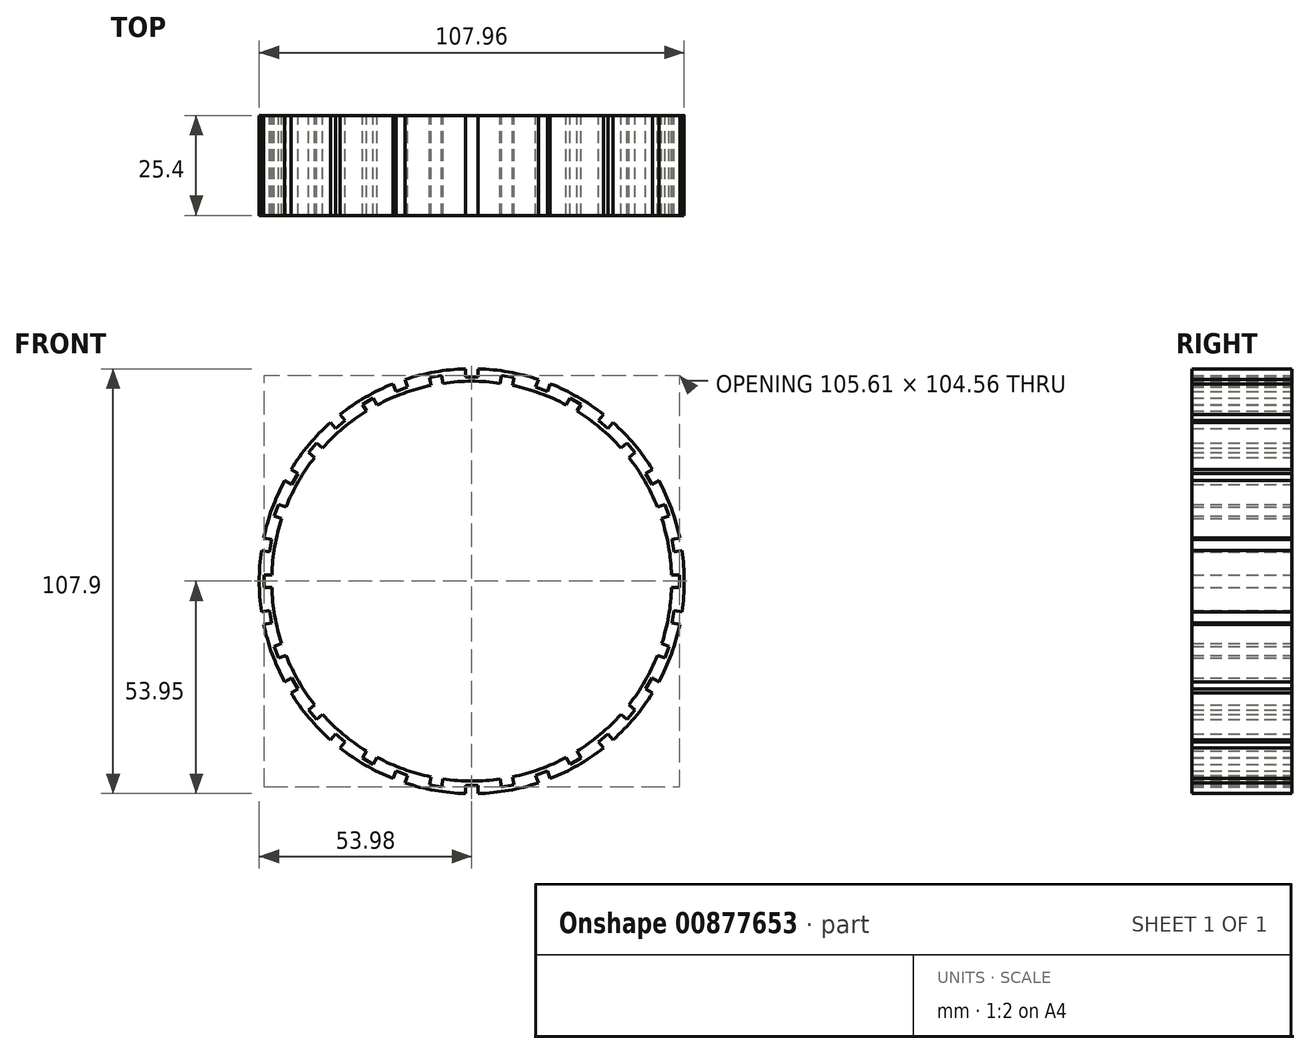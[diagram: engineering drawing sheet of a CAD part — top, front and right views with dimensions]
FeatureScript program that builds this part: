
annotation { "Feature Type Name" : "Feature", "Feature Type Description" : "" }
export const myFeature = defineFeature(function(context is Context, id is Id, definition is map)
    precondition{}
    {
        {
            var Q0;
            Q0=qCreatedBy(makeId("Front.planeOp"),FACE);
            var sketch = newSketch(context, id + "F0", { "sketchPlane" : qUnion([Q0])});
            skArc(sketch, "E0", {"start": v(-1.59, 53.95) * mm, "mid": v(-9.37, 53.15) * mm, "end": v(-16.96, 51.24) * mm});
            skArc(sketch, "E1", {"start": v(-50.78, -1.59) * mm, "mid": v(-50.03, -8.82) * mm, "end": v(-48.26, -15.87) * mm});
            skLineSegment(sketch, "E2", {"start": v(-1.59, 53.95) * mm, "end": v(-1.59, 51.92) * mm});
            skLineSegment(sketch, "E3", {"start": v(-1.59, 51.92) * mm, "end": v(1.59, 51.92) * mm});
            skLineSegment(sketch, "E4", {"start": v(1.59, 51.92) * mm, "end": v(1.59, 53.95) * mm});
            skLineSegment(sketch, "E5.1.0", {"start": v(-19.25, 48.25) * mm, "end": v(-16.27, 49.33) * mm});
            skLineSegment(sketch, "E5.1.1", {"start": v(-16.27, 49.33) * mm, "end": v(-16.96, 51.24) * mm});
            skLineSegment(sketch, "E5.1.2", {"start": v(-19.94, 50.16) * mm, "end": v(-19.25, 48.25) * mm});
            skLineSegment(sketch, "E5.2.0", {"start": v(-34.59, 38.75) * mm, "end": v(-32.16, 40.8) * mm});
            skLineSegment(sketch, "E5.2.1", {"start": v(-32.16, 40.8) * mm, "end": v(-33.46, 42.35) * mm});
            skLineSegment(sketch, "E5.2.2", {"start": v(-35.9, 40.3) * mm, "end": v(-34.59, 38.75) * mm});
            skLineSegment(sketch, "E5.3.0", {"start": v(-45.76, 24.59) * mm, "end": v(-44.17, 27.33) * mm});
            skLineSegment(sketch, "E5.3.1", {"start": v(-44.17, 27.33) * mm, "end": v(-45.93, 28.35) * mm});
            skLineSegment(sketch, "E5.3.2", {"start": v(-47.52, 25.6) * mm, "end": v(-45.76, 24.59) * mm});
            skLineSegment(sketch, "E5.4.0", {"start": v(-51.4, 7.45) * mm, "end": v(-50.86, 10.58) * mm});
            skLineSegment(sketch, "E5.4.1", {"start": v(-50.86, 10.58) * mm, "end": v(-52.86, 10.93) * mm});
            skLineSegment(sketch, "E5.4.2", {"start": v(-53.4, 7.8) * mm, "end": v(-51.4, 7.45) * mm});
            skLineSegment(sketch, "E5.5.0", {"start": v(-50.86, -10.58) * mm, "end": v(-51.4, -7.45) * mm});
            skLineSegment(sketch, "E5.5.1", {"start": v(-51.4, -7.45) * mm, "end": v(-53.4, -7.8) * mm});
            skLineSegment(sketch, "E5.5.2", {"start": v(-52.86, -10.93) * mm, "end": v(-50.86, -10.58) * mm});
            skLineSegment(sketch, "E5.6.0", {"start": v(-44.17, -27.33) * mm, "end": v(-45.76, -24.59) * mm});
            skLineSegment(sketch, "E5.6.1", {"start": v(-45.76, -24.59) * mm, "end": v(-47.52, -25.6) * mm});
            skLineSegment(sketch, "E5.6.2", {"start": v(-45.93, -28.35) * mm, "end": v(-44.17, -27.33) * mm});
            skLineSegment(sketch, "E5.7.0", {"start": v(-32.16, -40.8) * mm, "end": v(-34.59, -38.75) * mm});
            skLineSegment(sketch, "E5.7.1", {"start": v(-34.59, -38.75) * mm, "end": v(-35.9, -40.3) * mm});
            skLineSegment(sketch, "E5.7.2", {"start": v(-33.46, -42.35) * mm, "end": v(-32.16, -40.8) * mm});
            skLineSegment(sketch, "E5.8.0", {"start": v(-16.27, -49.33) * mm, "end": v(-19.25, -48.25) * mm});
            skLineSegment(sketch, "E5.8.1", {"start": v(-19.25, -48.25) * mm, "end": v(-19.94, -50.16) * mm});
            skLineSegment(sketch, "E5.8.2", {"start": v(-16.96, -51.24) * mm, "end": v(-16.27, -49.33) * mm});
            skLineSegment(sketch, "E5.9.0", {"start": v(1.59, -51.92) * mm, "end": v(-1.59, -51.92) * mm});
            skLineSegment(sketch, "E5.9.1", {"start": v(-1.59, -51.92) * mm, "end": v(-1.59, -53.95) * mm});
            skLineSegment(sketch, "E5.9.2", {"start": v(1.59, -53.95) * mm, "end": v(1.59, -51.92) * mm});
            skLineSegment(sketch, "E5.10.0", {"start": v(19.25, -48.25) * mm, "end": v(16.27, -49.33) * mm});
            skLineSegment(sketch, "E5.10.1", {"start": v(16.27, -49.33) * mm, "end": v(16.96, -51.24) * mm});
            skLineSegment(sketch, "E5.10.2", {"start": v(19.94, -50.16) * mm, "end": v(19.25, -48.25) * mm});
            skLineSegment(sketch, "E5.11.0", {"start": v(34.59, -38.75) * mm, "end": v(32.16, -40.8) * mm});
            skLineSegment(sketch, "E5.11.1", {"start": v(32.16, -40.8) * mm, "end": v(33.46, -42.35) * mm});
            skLineSegment(sketch, "E5.11.2", {"start": v(35.9, -40.3) * mm, "end": v(34.59, -38.75) * mm});
            skLineSegment(sketch, "E5.12.0", {"start": v(45.76, -24.59) * mm, "end": v(44.17, -27.33) * mm});
            skLineSegment(sketch, "E5.12.1", {"start": v(44.17, -27.33) * mm, "end": v(45.93, -28.35) * mm});
            skLineSegment(sketch, "E5.12.2", {"start": v(47.52, -25.6) * mm, "end": v(45.76, -24.59) * mm});
            skLineSegment(sketch, "E5.13.0", {"start": v(51.4, -7.45) * mm, "end": v(50.86, -10.58) * mm});
            skLineSegment(sketch, "E5.13.1", {"start": v(50.86, -10.58) * mm, "end": v(52.86, -10.93) * mm});
            skLineSegment(sketch, "E5.13.2", {"start": v(53.4, -7.8) * mm, "end": v(51.4, -7.45) * mm});
            skLineSegment(sketch, "E5.14.0", {"start": v(50.86, 10.58) * mm, "end": v(51.4, 7.45) * mm});
            skLineSegment(sketch, "E5.14.1", {"start": v(51.4, 7.45) * mm, "end": v(53.4, 7.8) * mm});
            skLineSegment(sketch, "E5.14.2", {"start": v(52.86, 10.93) * mm, "end": v(50.86, 10.58) * mm});
            skLineSegment(sketch, "E5.15.0", {"start": v(44.17, 27.33) * mm, "end": v(45.76, 24.59) * mm});
            skLineSegment(sketch, "E5.15.1", {"start": v(45.76, 24.59) * mm, "end": v(47.52, 25.6) * mm});
            skLineSegment(sketch, "E5.15.2", {"start": v(45.93, 28.35) * mm, "end": v(44.17, 27.33) * mm});
            skLineSegment(sketch, "E5.16.0", {"start": v(32.16, 40.8) * mm, "end": v(34.59, 38.75) * mm});
            skLineSegment(sketch, "E5.16.1", {"start": v(34.59, 38.75) * mm, "end": v(35.9, 40.3) * mm});
            skLineSegment(sketch, "E5.16.2", {"start": v(33.46, 42.35) * mm, "end": v(32.16, 40.8) * mm});
            skLineSegment(sketch, "E5.17.0", {"start": v(16.27, 49.33) * mm, "end": v(19.25, 48.25) * mm});
            skLineSegment(sketch, "E5.17.1", {"start": v(19.25, 48.25) * mm, "end": v(19.94, 50.16) * mm});
            skLineSegment(sketch, "E5.17.2", {"start": v(16.96, 51.24) * mm, "end": v(16.27, 49.33) * mm});
            skArc(sketch, "E6.trimOffspring", {"start": v(16.96, 51.24) * mm, "mid": v(9.37, 53.15) * mm, "end": v(1.59, 53.95) * mm});
            skArc(sketch, "E7.trimOffspring", {"start": v(33.46, 42.35) * mm, "mid": v(26.99, 46.74) * mm, "end": v(19.94, 50.16) * mm});
            skArc(sketch, "E8.trimOffspring", {"start": v(45.93, 28.35) * mm, "mid": v(41.35, 34.7) * mm, "end": v(35.9, 40.3) * mm});
            skArc(sketch, "E9.trimOffspring", {"start": v(52.86, 10.93) * mm, "mid": v(50.72, 18.46) * mm, "end": v(47.52, 25.6) * mm});
            skArc(sketch, "E10.trimOffspring", {"start": v(53.4, -7.8) * mm, "mid": v(53.97, 0) * mm, "end": v(53.4, 7.8) * mm});
            skArc(sketch, "E11.trimOffspring", {"start": v(47.52, -25.6) * mm, "mid": v(50.72, -18.46) * mm, "end": v(52.86, -10.93) * mm});
            skArc(sketch, "E12.trimOffspring", {"start": v(35.9, -40.3) * mm, "mid": v(41.35, -34.7) * mm, "end": v(45.93, -28.35) * mm});
            skArc(sketch, "E13.trimOffspring", {"start": v(19.94, -50.16) * mm, "mid": v(26.99, -46.74) * mm, "end": v(33.46, -42.35) * mm});
            skArc(sketch, "E14.trimOffspring", {"start": v(1.59, -53.95) * mm, "mid": v(9.37, -53.15) * mm, "end": v(16.96, -51.24) * mm});
            skArc(sketch, "E15.trimOffspring", {"start": v(-16.96, -51.24) * mm, "mid": v(-9.37, -53.15) * mm, "end": v(-1.59, -53.95) * mm});
            skArc(sketch, "E16.trimOffspring", {"start": v(-33.46, -42.35) * mm, "mid": v(-26.99, -46.74) * mm, "end": v(-19.94, -50.16) * mm});
            skArc(sketch, "E17.trimOffspring", {"start": v(-45.93, -28.35) * mm, "mid": v(-41.35, -34.7) * mm, "end": v(-35.9, -40.3) * mm});
            skArc(sketch, "E18.trimOffspring", {"start": v(-52.86, -10.93) * mm, "mid": v(-50.72, -18.46) * mm, "end": v(-47.52, -25.6) * mm});
            skArc(sketch, "E19.trimOffspring", {"start": v(-53.4, 7.8) * mm, "mid": v(-53.97, 0) * mm, "end": v(-53.4, -7.8) * mm});
            skArc(sketch, "E20.trimOffspring", {"start": v(-47.52, 25.6) * mm, "mid": v(-50.72, 18.46) * mm, "end": v(-52.86, 10.93) * mm});
            skArc(sketch, "E21.trimOffspring", {"start": v(-35.9, 40.3) * mm, "mid": v(-41.35, 34.7) * mm, "end": v(-45.93, 28.35) * mm});
            skArc(sketch, "E22.trimOffspring", {"start": v(-19.94, 50.16) * mm, "mid": v(-26.99, 46.74) * mm, "end": v(-33.46, 42.35) * mm});
            skLineSegment(sketch, "E23", {"start": v(-50.78, 1.59) * mm, "end": v(-52.8, 1.59) * mm});
            skLineSegment(sketch, "E24", {"start": v(-52.8, 1.59) * mm, "end": v(-52.8, -1.59) * mm});
            skLineSegment(sketch, "E25", {"start": v(-52.8, -1.59) * mm, "end": v(-50.78, -1.59) * mm});
            skLineSegment(sketch, "E26.1.0", {"start": v(-49.08, -19.55) * mm, "end": v(-47.17, -18.86) * mm});
            skLineSegment(sketch, "E26.1.1", {"start": v(-50.17, -16.57) * mm, "end": v(-49.08, -19.55) * mm});
            skLineSegment(sketch, "E26.1.2", {"start": v(-48.26, -15.87) * mm, "end": v(-50.17, -16.57) * mm});
            skLineSegment(sketch, "E26.2.0", {"start": v(-39.43, -35.16) * mm, "end": v(-37.88, -33.85) * mm});
            skLineSegment(sketch, "E26.2.1", {"start": v(-41.47, -32.73) * mm, "end": v(-39.43, -35.16) * mm});
            skLineSegment(sketch, "E26.2.2", {"start": v(-39.92, -31.42) * mm, "end": v(-41.47, -32.73) * mm});
            skLineSegment(sketch, "E26.3.0", {"start": v(-25.03, -46.53) * mm, "end": v(-24.01, -44.77) * mm});
            skLineSegment(sketch, "E26.3.1", {"start": v(-27.78, -44.94) * mm, "end": v(-25.03, -46.53) * mm});
            skLineSegment(sketch, "E26.3.2", {"start": v(-26.76, -43.18) * mm, "end": v(-27.78, -44.94) * mm});
            skLineSegment(sketch, "E26.4.0", {"start": v(-7.6, -52.28) * mm, "end": v(-7.25, -50.28) * mm});
            skLineSegment(sketch, "E26.4.1", {"start": v(-10.73, -51.73) * mm, "end": v(-7.6, -52.28) * mm});
            skLineSegment(sketch, "E26.4.2", {"start": v(-10.38, -49.73) * mm, "end": v(-10.73, -51.73) * mm});
            skLineSegment(sketch, "E26.5.0", {"start": v(10.73, -51.73) * mm, "end": v(10.38, -49.73) * mm});
            skLineSegment(sketch, "E26.5.1", {"start": v(7.6, -52.28) * mm, "end": v(10.73, -51.73) * mm});
            skLineSegment(sketch, "E26.5.2", {"start": v(7.25, -50.28) * mm, "end": v(7.6, -52.28) * mm});
            skLineSegment(sketch, "E26.6.0", {"start": v(27.78, -44.94) * mm, "end": v(26.76, -43.18) * mm});
            skLineSegment(sketch, "E26.6.1", {"start": v(25.03, -46.53) * mm, "end": v(27.78, -44.94) * mm});
            skLineSegment(sketch, "E26.6.2", {"start": v(24.01, -44.77) * mm, "end": v(25.03, -46.53) * mm});
            skLineSegment(sketch, "E26.7.0", {"start": v(41.47, -32.73) * mm, "end": v(39.92, -31.42) * mm});
            skLineSegment(sketch, "E26.7.1", {"start": v(39.43, -35.16) * mm, "end": v(41.47, -32.73) * mm});
            skLineSegment(sketch, "E26.7.2", {"start": v(37.88, -33.85) * mm, "end": v(39.43, -35.16) * mm});
            skLineSegment(sketch, "E26.8.0", {"start": v(50.17, -16.57) * mm, "end": v(48.26, -15.87) * mm});
            skLineSegment(sketch, "E26.8.1", {"start": v(49.08, -19.55) * mm, "end": v(50.17, -16.57) * mm});
            skLineSegment(sketch, "E26.8.2", {"start": v(47.17, -18.86) * mm, "end": v(49.08, -19.55) * mm});
            skLineSegment(sketch, "E26.9.0", {"start": v(52.8, 1.59) * mm, "end": v(50.78, 1.59) * mm});
            skLineSegment(sketch, "E26.9.1", {"start": v(52.8, -1.59) * mm, "end": v(52.8, 1.59) * mm});
            skLineSegment(sketch, "E26.9.2", {"start": v(50.78, -1.59) * mm, "end": v(52.8, -1.59) * mm});
            skLineSegment(sketch, "E26.10.0", {"start": v(49.08, 19.55) * mm, "end": v(47.17, 18.86) * mm});
            skLineSegment(sketch, "E26.10.1", {"start": v(50.17, 16.57) * mm, "end": v(49.08, 19.55) * mm});
            skLineSegment(sketch, "E26.10.2", {"start": v(48.26, 15.87) * mm, "end": v(50.17, 16.57) * mm});
            skLineSegment(sketch, "E26.11.0", {"start": v(39.43, 35.16) * mm, "end": v(37.88, 33.85) * mm});
            skLineSegment(sketch, "E26.11.1", {"start": v(41.47, 32.73) * mm, "end": v(39.43, 35.16) * mm});
            skLineSegment(sketch, "E26.11.2", {"start": v(39.92, 31.42) * mm, "end": v(41.47, 32.73) * mm});
            skLineSegment(sketch, "E26.12.0", {"start": v(25.03, 46.53) * mm, "end": v(24.01, 44.77) * mm});
            skLineSegment(sketch, "E26.12.1", {"start": v(27.78, 44.94) * mm, "end": v(25.03, 46.53) * mm});
            skLineSegment(sketch, "E26.12.2", {"start": v(26.76, 43.18) * mm, "end": v(27.78, 44.94) * mm});
            skLineSegment(sketch, "E26.13.0", {"start": v(7.6, 52.28) * mm, "end": v(7.25, 50.28) * mm});
            skLineSegment(sketch, "E26.13.1", {"start": v(10.73, 51.73) * mm, "end": v(7.6, 52.28) * mm});
            skLineSegment(sketch, "E26.13.2", {"start": v(10.38, 49.73) * mm, "end": v(10.73, 51.73) * mm});
            skLineSegment(sketch, "E26.14.0", {"start": v(-10.73, 51.73) * mm, "end": v(-10.38, 49.73) * mm});
            skLineSegment(sketch, "E26.14.1", {"start": v(-7.6, 52.28) * mm, "end": v(-10.73, 51.73) * mm});
            skLineSegment(sketch, "E26.14.2", {"start": v(-7.25, 50.28) * mm, "end": v(-7.6, 52.28) * mm});
            skLineSegment(sketch, "E26.15.0", {"start": v(-27.78, 44.94) * mm, "end": v(-26.76, 43.18) * mm});
            skLineSegment(sketch, "E26.15.1", {"start": v(-25.03, 46.53) * mm, "end": v(-27.78, 44.94) * mm});
            skLineSegment(sketch, "E26.15.2", {"start": v(-24.01, 44.77) * mm, "end": v(-25.03, 46.53) * mm});
            skLineSegment(sketch, "E26.16.0", {"start": v(-41.47, 32.73) * mm, "end": v(-39.92, 31.42) * mm});
            skLineSegment(sketch, "E26.16.1", {"start": v(-39.43, 35.16) * mm, "end": v(-41.47, 32.73) * mm});
            skLineSegment(sketch, "E26.16.2", {"start": v(-37.88, 33.85) * mm, "end": v(-39.43, 35.16) * mm});
            skLineSegment(sketch, "E26.17.0", {"start": v(-50.17, 16.57) * mm, "end": v(-48.26, 15.87) * mm});
            skLineSegment(sketch, "E26.17.1", {"start": v(-49.08, 19.55) * mm, "end": v(-50.17, 16.57) * mm});
            skLineSegment(sketch, "E26.17.2", {"start": v(-47.17, 18.86) * mm, "end": v(-49.08, 19.55) * mm});
            skArc(sketch, "E27.trimOffspring", {"start": v(-48.26, 15.87) * mm, "mid": v(-50.03, 8.82) * mm, "end": v(-50.78, 1.59) * mm});
            skArc(sketch, "E28.trimOffspring", {"start": v(-39.92, 31.42) * mm, "mid": v(-44, 25.4) * mm, "end": v(-47.17, 18.86) * mm});
            skArc(sketch, "E29.trimOffspring", {"start": v(-26.76, 43.18) * mm, "mid": v(-32.65, 38.92) * mm, "end": v(-37.88, 33.85) * mm});
            skArc(sketch, "E30.trimOffspring", {"start": v(-10.38, 49.73) * mm, "mid": v(-17.37, 47.74) * mm, "end": v(-24.01, 44.77) * mm});
            skArc(sketch, "E31.trimOffspring", {"start": v(7.25, 50.28) * mm, "mid": v(0, 50.8) * mm, "end": v(-7.25, 50.28) * mm});
            skArc(sketch, "E32.trimOffspring", {"start": v(24.01, 44.77) * mm, "mid": v(17.37, 47.74) * mm, "end": v(10.38, 49.73) * mm});
            skArc(sketch, "E33.trimOffspring", {"start": v(37.88, 33.85) * mm, "mid": v(32.65, 38.92) * mm, "end": v(26.76, 43.18) * mm});
            skArc(sketch, "E34.trimOffspring", {"start": v(47.17, 18.86) * mm, "mid": v(44, 25.4) * mm, "end": v(39.92, 31.42) * mm});
            skArc(sketch, "E35.trimOffspring", {"start": v(50.78, 1.59) * mm, "mid": v(50.03, 8.82) * mm, "end": v(48.26, 15.87) * mm});
            skArc(sketch, "E36.trimOffspring", {"start": v(48.26, -15.87) * mm, "mid": v(50.03, -8.82) * mm, "end": v(50.78, -1.59) * mm});
            skArc(sketch, "E37.trimOffspring", {"start": v(39.92, -31.42) * mm, "mid": v(44, -25.4) * mm, "end": v(47.17, -18.86) * mm});
            skArc(sketch, "E38.trimOffspring", {"start": v(26.76, -43.18) * mm, "mid": v(32.65, -38.92) * mm, "end": v(37.88, -33.85) * mm});
            skArc(sketch, "E39.trimOffspring", {"start": v(10.38, -49.73) * mm, "mid": v(17.37, -47.74) * mm, "end": v(24.01, -44.77) * mm});
            skArc(sketch, "E40.trimOffspring", {"start": v(-7.25, -50.28) * mm, "mid": v(0, -50.8) * mm, "end": v(7.25, -50.28) * mm});
            skArc(sketch, "E41.trimOffspring", {"start": v(-24.01, -44.77) * mm, "mid": v(-17.37, -47.74) * mm, "end": v(-10.38, -49.73) * mm});
            skArc(sketch, "E42.trimOffspring", {"start": v(-37.88, -33.85) * mm, "mid": v(-32.65, -38.92) * mm, "end": v(-26.76, -43.18) * mm});
            skArc(sketch, "E43.trimOffspring", {"start": v(-47.17, -18.86) * mm, "mid": v(-44, -25.4) * mm, "end": v(-39.92, -31.42) * mm});
            skSolve(sketch);
        }
        {
            var Q0;
            Q0 = qSketchRegion(id + "F0", true);
            extrude(context, id + "F1", {"entities" : qUnion([Q0]), "depth" : 25.4 * mm, "offsetDistance" : 25.4 * mm});
        }
    });
